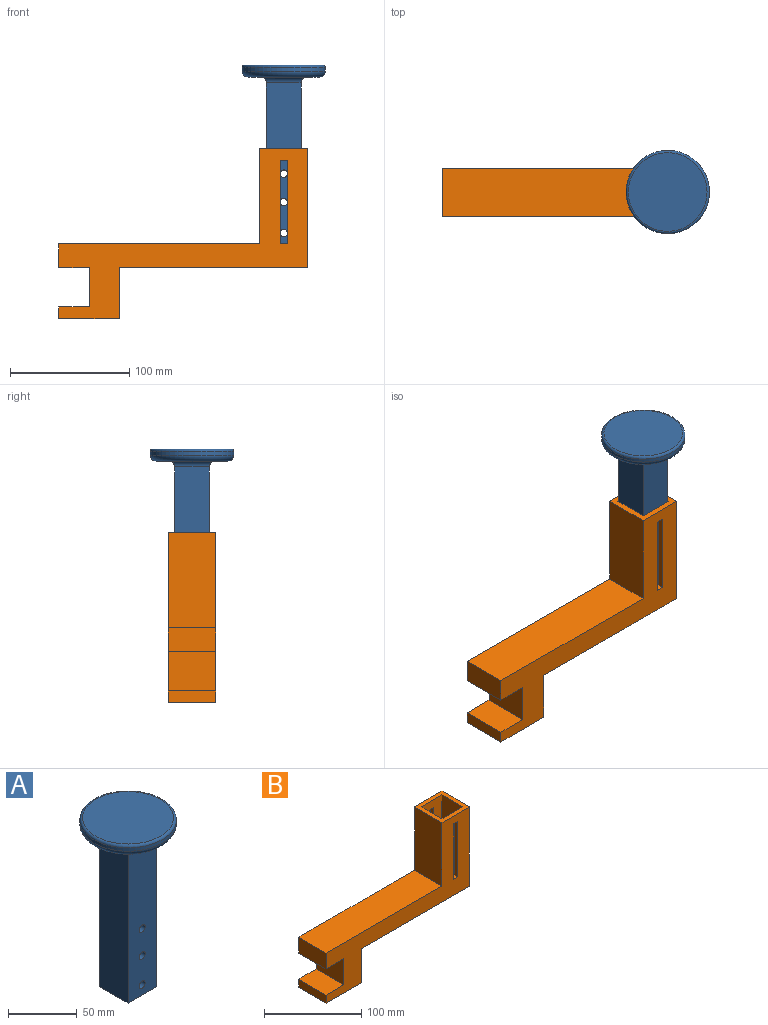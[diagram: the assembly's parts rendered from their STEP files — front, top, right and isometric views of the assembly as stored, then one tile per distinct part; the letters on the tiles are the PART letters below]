
ASSEMBLY  parts=2 mates=1
PART A: 17 faces, bbox 75.8x75.8x150 mm
  f0: plane 135x29mm, normal (0,-1,0), area 3824.4mm2, adj f1,f3,f4,f5,f6,f7,f11
  f1: plane 135x29mm, normal (1,0,0), area 3915mm2, adj f0,f2,f4,f12
  f2: plane 135x29mm, normal (0,1,0), area 3824.4mm2, adj f1,f3,f4,f5,f6,f7,f14
  f3: plane 135x29mm, normal (-1,0,0), area 3915mm2, adj f0,f2,f4,f13
  f4: plane 29x29mm, normal (0,0,-1), area 841mm2, adj f0,f1,f2,f3
  f5: cylinder r=3.1mm len=29mm, axis (0,-1,0), area 564.9mm2, adj f0,f2
  f6: cylinder r=3.1mm len=29mm, axis (0,-1,0), area 564.9mm2, adj f0,f2
  f7: cylinder r=3.1mm len=29mm, axis (0,-1,0), area 564.9mm2, adj f0,f2
  f8: cylinder r=35mm len=70mm, axis (0,0,-1), area 659.7mm2, adj f15,f16
  f9: plane 66x66mm, normal (0,0,1), area 3421.2mm2, adj f16
  f10: plane 60x60mm, normal (0,0,-1), area 1306.4mm2, adj f11,f12,f13,f14,f15
  f11: cylinder r=5mm len=39mm, axis (-1,0,0), area 256.3mm2, adj f0,f10,f12,f13
  f12: cylinder r=5mm len=39mm, axis (0,-1,0), area 256.3mm2, adj f1,f10,f11,f14
  f13: cylinder r=5mm len=39mm, axis (0,1,0), area 256.3mm2, adj f3,f10,f11,f14
  f14: cylinder r=5mm len=39mm, axis (1,0,0), area 256.3mm2, adj f2,f10,f12,f13
  f15: torus R=30mm, axis (0,0,1), area 1637.5mm2, adj f8,f10
  f16: torus R=33mm, axis (0,0,1), area 676.5mm2, adj f8,f9
PART B: 25 faces, bbox 209x40x143 mm
  f0: plane 70x5mm, normal (1,0,0), area 350mm2, adj f1,f14,f19,f24
  f1: plane 6x5mm, normal (0,0,-1), area 30mm2, adj f0,f2,f19,f24
  f2: plane 70x5mm, normal (-1,0,0), area 350mm2, adj f1,f14,f19,f24
  f3: plane 100x40mm, normal (1,0,0), area 4000mm2, adj f4,f18,f19,f20
  f4: plane 40x40mm, normal (0,0,1), area 700mm2, adj f3,f5,f19,f20,f21,f22,f23,f24
  f5: plane 80x40mm, normal (-1,0,0), area 3200mm2, adj f4,f6,f19,f20
  f6: plane 169x40mm, normal (0,0,1), area 6760mm2, adj f5,f7,f19,f20
  f7: plane 40x20mm, normal (-1,0,0), area 800mm2, adj f6,f8,f19,f20
  f8: plane 40x26mm, normal (0,0,-1), area 1040mm2, adj f7,f9,f19,f20
  f9: plane 40x33mm, normal (-1,0,0), area 1320mm2, adj f8,f10,f19,f20
  f10: plane 40x26mm, normal (0,0,1), area 1040mm2, adj f9,f11,f19,f20
  f11: plane 40x10mm, normal (-1,0,0), area 400mm2, adj f10,f12,f19,f20
  f12: plane 51x40mm, normal (0,0,-1), area 2040mm2, adj f11,f13,f19,f20
  f13: plane 43x40mm, normal (1,0,0), area 1720mm2, adj f12,f18,f19,f20
  f14: plane 40x30mm, normal (0,0,1), area 960mm2, adj f0,f2,f15,f17,f19,f20,f21,f22
  f15: plane 70x5mm, normal (1,0,0), area 350mm2, adj f14,f16,f20,f21
  f16: plane 6x5mm, normal (0,0,-1), area 30mm2, adj f15,f17,f20,f21
  f17: plane 70x5mm, normal (-1,0,0), area 350mm2, adj f14,f16,f20,f21
  f18: plane 158x40mm, normal (0,0,-1), area 6320mm2, adj f3,f13,f19,f20
  f19: plane 209x143mm, normal (0,-1,0), area 8295mm2, adj f0,f1,f2,f3,f4,f5,f6,f7
  f20: plane 209x143mm, normal (0,1,0), area 8295mm2, adj f3,f4,f5,f6,f7,f8,f9,f10
  f21: plane 80x30mm, normal (0,-1,0), area 1980mm2, adj f4,f14,f15,f16,f17,f22,f23
  f22: plane 80x30mm, normal (-1,0,0), area 2400mm2, adj f4,f14,f21,f24
  f23: plane 80x30mm, normal (1,0,0), area 2400mm2, adj f4,f14,f21,f24
  f24: plane 80x30mm, normal (0,1,0), area 1980mm2, adj f0,f1,f2,f4,f14,f22,f23
PLACE A rot(axis=(-0.01,1,-0.02),0deg) t=(80.41,41.12,-64.55)mm
PLACE B rot(axis=(-0.01,1,-0.02),0deg) t=(-82.59,41.12,-127.55)mm
MATE slider A.f8 <-> B.f14  axis (0,0,-1) through (80.41,41.12,-64.55)mm
